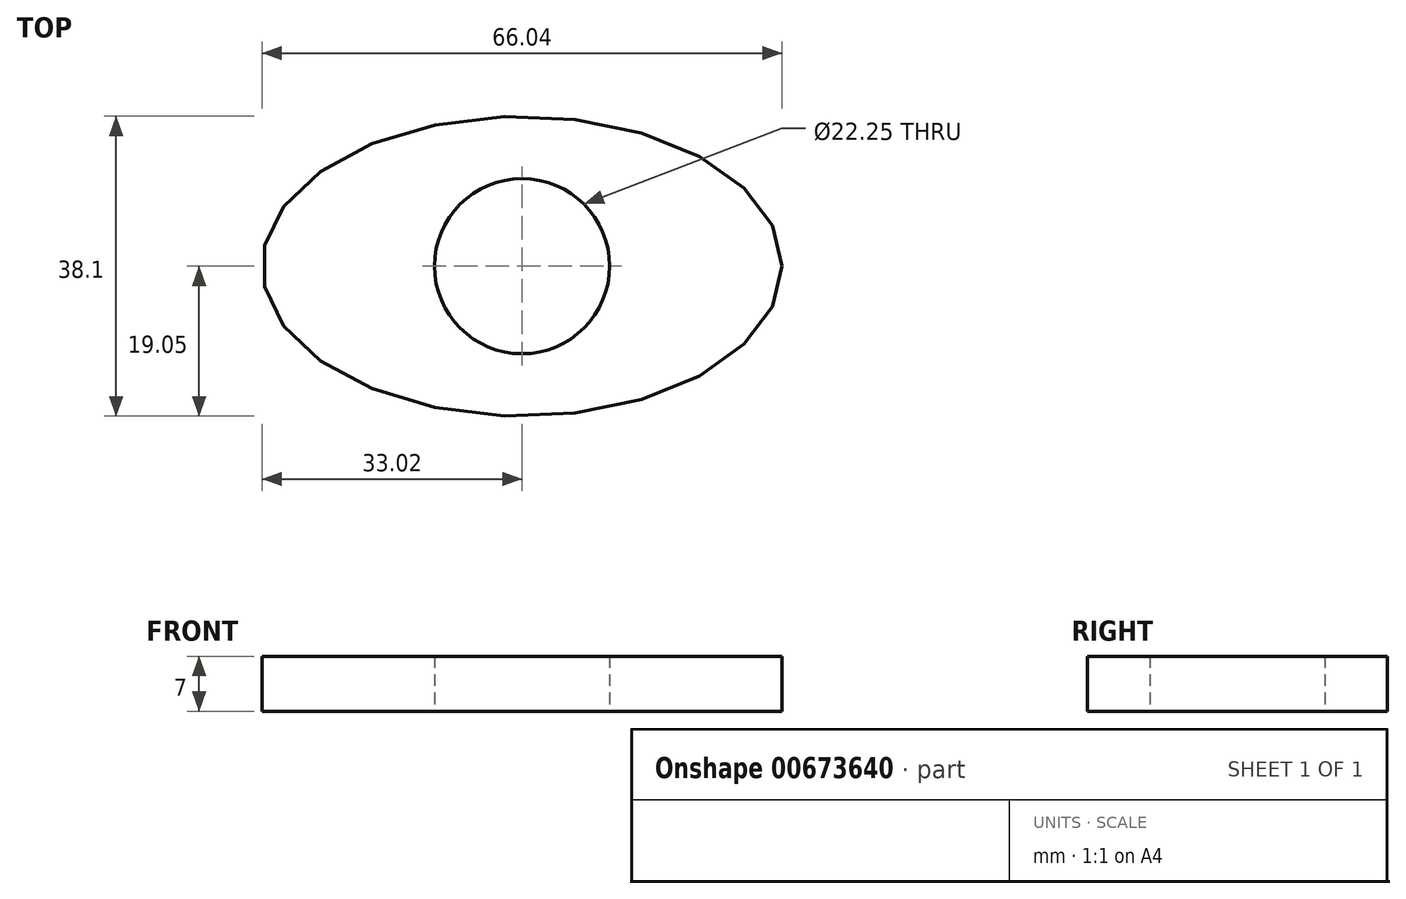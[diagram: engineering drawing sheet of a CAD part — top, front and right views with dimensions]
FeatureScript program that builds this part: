
annotation { "Feature Type Name" : "Feature", "Feature Type Description" : "" }
export const myFeature = defineFeature(function(context is Context, id is Id, definition is map)
    precondition{}
    {
        {
            var Q0;
            Q0=qCreatedBy(makeId("Top.planeOp"),FACE);
            var sketch = newSketch(context, id + "F0", { "sketchPlane" : qUnion([Q0])});
            skEllipse(sketch, "E0", {"center": v(0, 0) * mm, "majorRadius": 33.02 * mm, "minorRadius": 19.05 * mm, "majorAxis": v(1, 0)});
            skCircle(sketch, "E1", {"center": v(0, 0) * mm, "radius": 11.12 * mm});
            skLineSegment(sketch, "E2", {"start": v(-33.02, 0) * mm, "end": v(33.02, 0) * mm, "construction": true});
            skLineSegment(sketch, "E3", {"start": v(0, 19.05) * mm, "end": v(0, -19.05) * mm, "construction": true});
            skSolve(sketch);
        }
        {
            var Q0;
            Q0=makeQuery(id+"F0.imprint","IMPRINT",FACE,{"disambiguationData":[TD([[makeQuery(id+"F0.imprint","IMPRINT",EDGE,{"derivedFrom":sQuery(id+"F0.wireOp",EDGE,"E0")}),1.0]])]});
            extrude(context, id + "F1", {"entities" : qUnion([Q0]), "depth" : 7 * mm, "offsetDistance" : 25.4 * mm});
        }
    });
